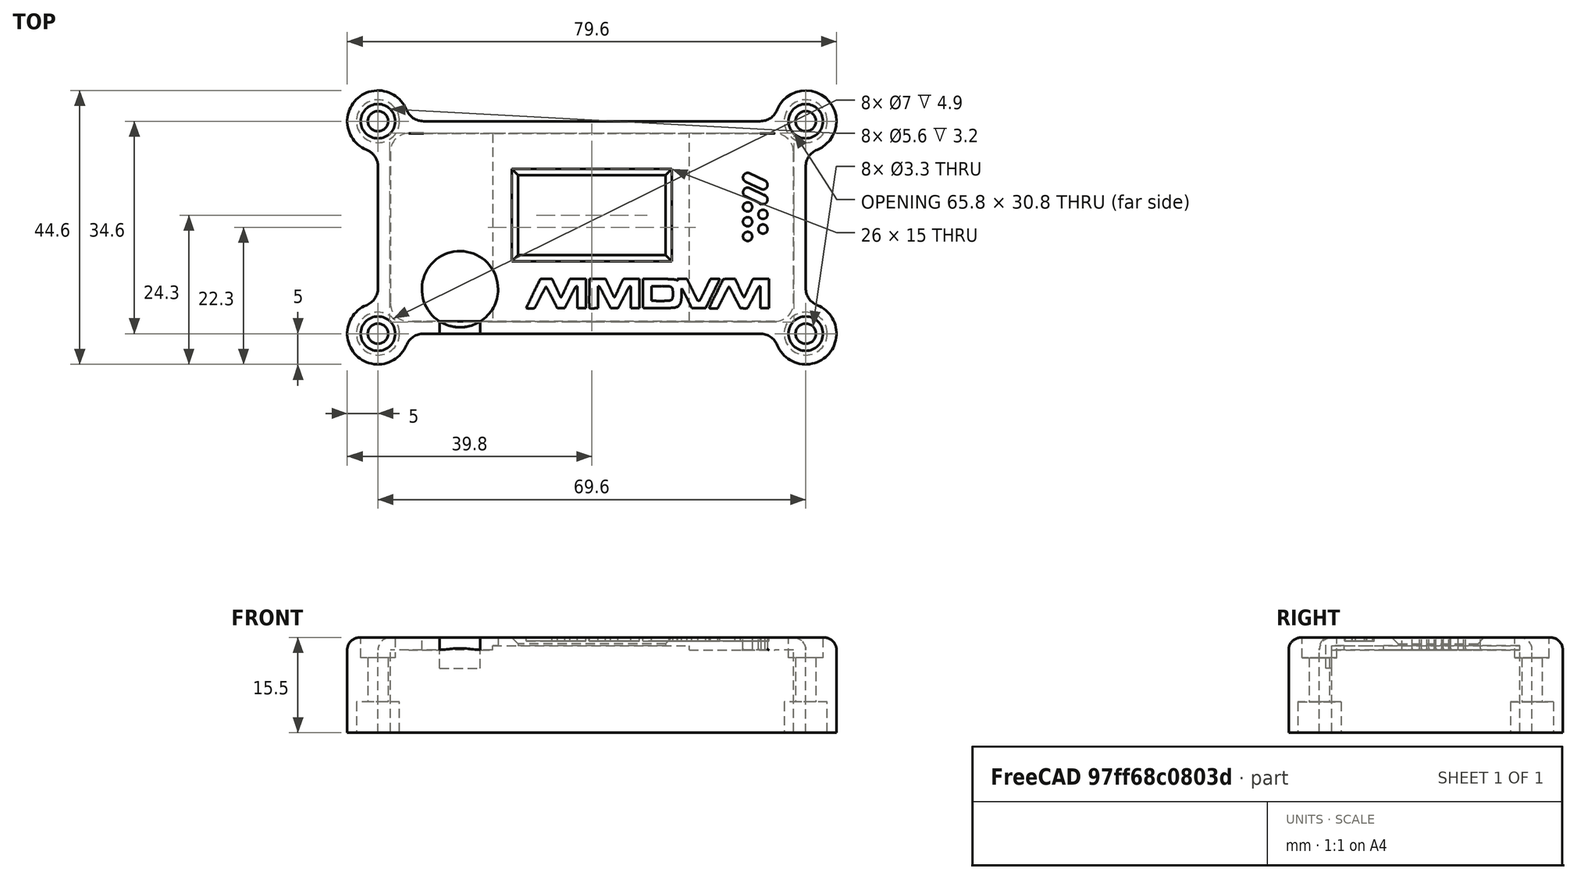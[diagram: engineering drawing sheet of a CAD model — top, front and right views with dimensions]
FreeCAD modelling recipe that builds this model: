
FCSTD DOCUMENT  (FreeCAD 0.18R13964 (Git))
Label: MMDVM_HS_Top-PCB-v1.7
License: CreativeCommons Attribution-NonCommercial-ShareAlike
LicenseURL: http://creativecommons.org/licenses/by-nc-sa/4.0/
objects: Sketcher::SketchObject×10, PartDesign::Pocket×6, Part::Feature×5, PartDesign::Fillet×4, Part::Cut×2, Part::FeaturePython×2, PartDesign::Pad×1, PartDesign::Chamfer×1, PartDesign::Hole×1, Part::MultiFuse×1, PartDesign::Body×1, Part::Extrusion×1, Mesh::Feature×1
note: 43 computed .brp shape members not serialized (recipe doc carries the construction recipe); baked Part::Feature solids carry a one-line shape summary decoded from their .brp

FEATURE [Sketcher::SketchObject] Sketch
  MapMode = 5
  Support = -> [XY_Plane]
  sketch-geometry (24):
    g0: LineSegment [constr] StartX=-32.5 StartY=15 StartZ=0 EndX=32.5 EndY=15 EndZ=0
    g1: LineSegment [constr] StartX=32.5 StartY=15 StartZ=0 EndX=32.5 EndY=-15 EndZ=0
    g2: LineSegment [constr] StartX=32.5 StartY=-15 StartZ=0 EndX=-32.5 EndY=-15 EndZ=0
    g3: LineSegment [constr] StartX=-32.5 StartY=-15 StartZ=0 EndX=-32.5 EndY=15 EndZ=0
    g4: LineSegment [constr] StartX=-29 StartY=11.5 StartZ=0 EndX=29 EndY=11.5 EndZ=0
    g5: LineSegment [constr] StartX=29 StartY=11.5 StartZ=0 EndX=29 EndY=-11.5 EndZ=0
    g6: LineSegment [constr] StartX=29 StartY=-11.5 StartZ=0 EndX=-29 EndY=-11.5 EndZ=0
    g7: LineSegment [constr] StartX=-29 StartY=-11.5 StartZ=0 EndX=-29 EndY=11.5 EndZ=0
    g8: Circle CenterX=-29 CenterY=11.5 CenterZ=0 NormalX=0 NormalY=0 NormalZ=1 AngleXU=0 Radius=1.375
    g9: Circle CenterX=29 CenterY=11.5 CenterZ=0 NormalX=0 NormalY=0 NormalZ=1 AngleXU=0 Radius=1.375
    g10: Circle CenterX=29 CenterY=-11.5 CenterZ=0 NormalX=0 NormalY=0 NormalZ=1 AngleXU=0 Radius=1.375
    g11: Circle CenterX=-29 CenterY=-11.5 CenterZ=0 NormalX=0 NormalY=0 NormalZ=1 AngleXU=0 Radius=1.375
    g12: LineSegment [constr] StartX=-29.5 StartY=12 StartZ=0 EndX=29.5 EndY=12 EndZ=0
    g13: LineSegment [constr] StartX=29.5 StartY=12 StartZ=0 EndX=29.5 EndY=-12 EndZ=0
    g14: LineSegment [constr] StartX=29.5 StartY=-12 StartZ=0 EndX=-29.5 EndY=-12 EndZ=0
    g15: LineSegment [constr] StartX=-29.5 StartY=-12 StartZ=0 EndX=-29.5 EndY=12 EndZ=0
    g16: ArcOfCircle CenterX=-29.5 CenterY=12 CenterZ=0 NormalX=0 NormalY=0 NormalZ=1 AngleXU=0 Radius=3 StartAngle=1.5708 EndAngle=3.1416
    g17: ArcOfCircle CenterX=29.5 CenterY=12 CenterZ=0 NormalX=0 NormalY=0 NormalZ=1 AngleXU=0 Radius=3 StartAngle=1.42077e-07 EndAngle=1.5708
    g18: ArcOfCircle CenterX=29.5 CenterY=-12 CenterZ=0 NormalX=0 NormalY=0 NormalZ=1 AngleXU=0 Radius=3 StartAngle=4.71239 EndAngle=6.28319
    g19: ArcOfCircle CenterX=-29.5 CenterY=-12 CenterZ=0 NormalX=0 NormalY=0 NormalZ=1 AngleXU=0 Radius=3 StartAngle=3.14159 EndAngle=4.71239
    g20: LineSegment StartX=-29.5 StartY=15 StartZ=0 EndX=29.5 EndY=15 EndZ=0
    g21: LineSegment StartX=32.5 StartY=12 StartZ=0 EndX=32.5 EndY=-12 EndZ=0
    g22: LineSegment StartX=29.5 StartY=-15 StartZ=0 EndX=-29.5 EndY=-15 EndZ=0
    g23: LineSegment StartX=-32.5 StartY=-12 StartZ=0 EndX=-32.5 EndY=12 EndZ=0
  constraints (68):
    c: Coincident(g0,g1)
    c: Coincident(g1,g2)
    c: Coincident(g2,g3)
    c: Coincident(g3,g0)
    c: Horizontal(g0)
    c: Horizontal(g2)
    c: Vertical(g1)
    c: Vertical(g3)
    c: DistanceX(g0,g0) = 65
    c: DistanceY(g1,g1) = 30
    c: Symmetric(g0,g0,g-2)
    c: Symmetric(g0,g1,g-1)
    c: Coincident(g4,g5)
    c: Coincident(g5,g6)
    c: Coincident(g6,g7)
    c: Coincident(g7,g4)
    c: Horizontal(g4)
    c: Horizontal(g6)
    c: Vertical(g5)
    c: Vertical(g7)
    c: DistanceX(g4,g4) = 58
    c: DistanceY(g5,g5) = 23
    c: Symmetric(g4,g5,g-1)
    c: Symmetric(g4,g4,g-2)
    c: Coincident(g8,g4)
    c: Coincident(g9,g4)
    c: Coincident(g10,g5)
    c: Coincident(g11,g6)
    c: Radius(g11) = 1.375
    c: Radius(g8) = 1.375
    c: Radius(g9) = 1.375
    c: Radius(g10) = 1.375
    c: Coincident(g12,g13)
    c: Coincident(g13,g14)
    c: Coincident(g14,g15)
    c: Coincident(g15,g12)
    c: Horizontal(g12)
    c: Horizontal(g14)
    c: Vertical(g13)
    c: Vertical(g15)
    c: DistanceX(g4,g12) = 0.5
    c: DistanceY(g4,g12) = 0.5
    c: DistanceY(g13,g5) = 0.5
    c: DistanceX(g14,g6) = 0.5
    c: Coincident(g16,g12)
    c: Radius(g16) = 3
    c: Coincident(g17,g12)
    c: Radius(g17) = 3
    c: Coincident(g18,g13)
    c: Radius(g18) = 3
    c: Coincident(g19,g14)
    c: Radius(g19) = 3
    c: PointOnObject(g16,g0)
    c: PointOnObject(g17,g1)
    c: PointOnObject(g18,g2)
    c: PointOnObject(g19,g3)
    c: Coincident(g20,g16)
    c: Horizontal(g20)
    c: Coincident(g20,g17)
    c: Coincident(g21,g17)
    c: Vertical(g21)
    c: Coincident(g18,g21)
    c: Coincident(g22,g18)
    c: Horizontal(g22)
    c: Coincident(g19,g22)
    c: Coincident(g23,g19)
    c: Vertical(g23)
    c: Coincident(g23,g16)
FEATURE [Sketcher::SketchObject] Sketch001
  MapMode = 5
  Support = -> [XY_Plane]
  expr: Constraints[8] = Sketch.Constraints[8]
  expr: Constraints[41] = Sketch.Constraints[41]
  expr: Constraints[9] = Sketch.Constraints[9]
  expr: Constraints[45] = Sketch.Constraints[45]
  expr: Constraints[43] = Sketch.Constraints[43]
  expr: Constraints[42] = Sketch.Constraints[42]
  expr: Constraints[20] = Sketch.Constraints[20]
  expr: Constraints[21] = Sketch.Constraints[21]
  expr: Constraints[28] = Sketch.Constraints[28]
  expr: Constraints[29] = Sketch.Constraints[29]
  expr: Constraints[30] = Sketch.Constraints[30]
  expr: Constraints[40] = Sketch.Constraints[40]
  expr: Constraints[31] = Sketch.Constraints[31]
  expr: Constraints[47] = Sketch.Constraints[47]
  expr: Constraints[49] = Sketch.Constraints[49]
  expr: Constraints[51] = Sketch.Constraints[51]
  sketch-geometry (64):
    g0: LineSegment [constr] StartX=-32.5 StartY=15 StartZ=0 EndX=32.5 EndY=15 EndZ=0
    g1: LineSegment [constr] StartX=32.5 StartY=15 StartZ=0 EndX=32.5 EndY=-15 EndZ=0
    g2: LineSegment [constr] StartX=32.5 StartY=-15 StartZ=0 EndX=-32.5 EndY=-15 EndZ=0
    g3: LineSegment [constr] StartX=-32.5 StartY=-15 StartZ=0 EndX=-32.5 EndY=15 EndZ=0
    g4: LineSegment [constr] StartX=-29 StartY=11.5 StartZ=0 EndX=29 EndY=11.5 EndZ=0
    g5: LineSegment [constr] StartX=29 StartY=11.5 StartZ=0 EndX=29 EndY=-11.5 EndZ=0
    g6: LineSegment [constr] StartX=29 StartY=-11.5 StartZ=0 EndX=-29 EndY=-11.5 EndZ=0
    g7: LineSegment [constr] StartX=-29 StartY=-11.5 StartZ=0 EndX=-29 EndY=11.5 EndZ=0
    g8: Circle [constr] CenterX=-29 CenterY=11.5 CenterZ=0 NormalX=0 NormalY=0 NormalZ=1 AngleXU=0 Radius=1.375
    g9: Circle [constr] CenterX=29 CenterY=11.5 CenterZ=0 NormalX=0 NormalY=0 NormalZ=1 AngleXU=0 Radius=1.375
    g10: Circle [constr] CenterX=29 CenterY=-11.5 CenterZ=0 NormalX=0 NormalY=0 NormalZ=1 AngleXU=0 Radius=1.375
    g11: Circle [constr] CenterX=-29 CenterY=-11.5 CenterZ=0 NormalX=0 NormalY=0 NormalZ=1 AngleXU=0 Radius=1.375
    g12: LineSegment [constr] StartX=-29.5 StartY=12 StartZ=0 EndX=29.5 EndY=12 EndZ=0
    g13: LineSegment [constr] StartX=29.5 StartY=12 StartZ=0 EndX=29.5 EndY=-12 EndZ=0
    g14: LineSegment [constr] StartX=29.5 StartY=-12 StartZ=0 EndX=-29.5 EndY=-12 EndZ=0
    g15: LineSegment [constr] StartX=-29.5 StartY=-12 StartZ=0 EndX=-29.5 EndY=12 EndZ=0
    g16: ArcOfCircle [constr] CenterX=-29.5 CenterY=12 CenterZ=0 NormalX=0 NormalY=0 NormalZ=1 AngleXU=0 Radius=3 StartAngle=1.5708 EndAngle=3.14159
    g17: ArcOfCircle [constr] CenterX=29.5 CenterY=12 CenterZ=0 NormalX=0 NormalY=0 NormalZ=1 AngleXU=0 Radius=3 StartAngle=2.8425e-08 EndAngle=1.5708
    g18: ArcOfCircle [constr] CenterX=29.5 CenterY=-12 CenterZ=0 NormalX=0 NormalY=0 NormalZ=1 AngleXU=0 Radius=3 StartAngle=4.71239 EndAngle=6.28319
    g19: ArcOfCircle [constr] CenterX=-29.5 CenterY=-12 CenterZ=0 NormalX=0 NormalY=0 NormalZ=1 AngleXU=0 Radius=3 StartAngle=3.14159 EndAngle=4.71239
    g20: LineSegment [constr] StartX=-29.5 StartY=15 StartZ=0 EndX=29.5 EndY=15 EndZ=0
    g21: LineSegment [constr] StartX=32.5 StartY=12 StartZ=0 EndX=32.5 EndY=-12 EndZ=0
    g22: LineSegment [constr] StartX=29.5 StartY=-15 StartZ=0 EndX=-29.5 EndY=-15 EndZ=0
    g23: LineSegment [constr] StartX=-32.5 StartY=-12 StartZ=0 EndX=-32.5 EndY=12 EndZ=0
    g24: ArcOfCircle [constr] CenterX=-29.5 CenterY=12 CenterZ=0 NormalX=0 NormalY=0 NormalZ=1 AngleXU=0 Radius=3.3 StartAngle=1.5708 EndAngle=3.14159
    g25: ArcOfCircle [constr] CenterX=29.5 CenterY=12 CenterZ=0 NormalX=0 NormalY=0 NormalZ=1 AngleXU=0 Radius=3.3 StartAngle=-2.2e-10 EndAngle=1.5708
    g26: ArcOfCircle [constr] CenterX=29.5 CenterY=-12 CenterZ=0 NormalX=0 NormalY=0 NormalZ=1 AngleXU=0 Radius=3.3 StartAngle=4.71239 EndAngle=6.28319
    g27: ArcOfCircle [constr] CenterX=-29.5 CenterY=-12 CenterZ=0 NormalX=0 NormalY=0 NormalZ=1 AngleXU=0 Radius=3.3 StartAngle=3.14159 EndAngle=4.71239
    g28: LineSegment [constr] StartX=-32.8 StartY=12 StartZ=0 EndX=-32.8 EndY=-12 EndZ=0
    g29: LineSegment [constr] StartX=-29.5 StartY=15.3 StartZ=0 EndX=29.5 EndY=15.3 EndZ=0
    g30: LineSegment [constr] StartX=32.8 StartY=12 StartZ=0 EndX=32.8 EndY=-12 EndZ=0
    g31: LineSegment [constr] StartX=29.5 StartY=-15.3 StartZ=0 EndX=-29.5 EndY=-15.3 EndZ=0
    g32: LineSegment [constr] StartX=-34.8 StartY=17.3 StartZ=0 EndX=34.8 EndY=17.3 EndZ=0
    g33: LineSegment [constr] StartX=34.8 StartY=17.3 StartZ=0 EndX=34.8 EndY=-17.3 EndZ=0
    g34: LineSegment [constr] StartX=34.8 StartY=-17.3 StartZ=0 EndX=-34.8 EndY=-17.3 EndZ=0
    g35: LineSegment [constr] StartX=-34.8 StartY=-17.3 StartZ=0 EndX=-34.8 EndY=17.3 EndZ=0
    g36: Circle [constr] CenterX=34.8 CenterY=17.3 CenterZ=0 NormalX=0 NormalY=0 NormalZ=1 AngleXU=0 Radius=5
    g37: Circle [constr] CenterX=34.8 CenterY=-17.3 CenterZ=0 NormalX=0 NormalY=0 NormalZ=1 AngleXU=0 Radius=5
    g38: Circle [constr] CenterX=-34.8 CenterY=-17.3 CenterZ=0 NormalX=0 NormalY=0 NormalZ=1 AngleXU=0 Radius=5
    g39: Circle [constr] CenterX=-34.8 CenterY=17.3 CenterZ=0 NormalX=0 NormalY=0 NormalZ=1 AngleXU=0 Radius=5
    g40: Circle [constr] CenterX=27.3838 CenterY=20.3 CenterZ=0 NormalX=0 NormalY=0 NormalZ=1 AngleXU=0 Radius=3
    g41: Circle [constr] CenterX=-27.3838 CenterY=20.3 CenterZ=0 NormalX=0 NormalY=0 NormalZ=1 AngleXU=0 Radius=3
    g42: Circle [constr] CenterX=-37.8 CenterY=9.8838 CenterZ=0 NormalX=0 NormalY=0 NormalZ=1 AngleXU=0 Radius=3
    g43: Circle [constr] CenterX=-37.8 CenterY=-9.8838 CenterZ=0 NormalX=0 NormalY=0 NormalZ=1 AngleXU=0 Radius=3
    g44: Circle [constr] CenterX=-27.3838 CenterY=-20.3 CenterZ=0 NormalX=0 NormalY=0 NormalZ=1 AngleXU=0 Radius=3
    g45: Circle [constr] CenterX=27.3838 CenterY=-20.3 CenterZ=0 NormalX=0 NormalY=0 NormalZ=1 AngleXU=0 Radius=3
    g46: Circle [constr] CenterX=37.8 CenterY=-9.8838 CenterZ=0 NormalX=0 NormalY=0 NormalZ=1 AngleXU=0 Radius=3
    g47: Circle [constr] CenterX=37.8 CenterY=9.8838 CenterZ=0 NormalX=0 NormalY=0 NormalZ=1 AngleXU=0 Radius=3
    g48: ArcOfCircle CenterX=34.8 CenterY=17.3 CenterZ=0 NormalX=0 NormalY=0 NormalZ=1 AngleXU=0 Radius=5 StartAngle=5.09679 EndAngle=9.04038
    g49: ArcOfCircle CenterX=27.3838 CenterY=20.3 CenterZ=0 NormalX=0 NormalY=0 NormalZ=1 AngleXU=0 Radius=3 StartAngle=4.71239 EndAngle=5.89879
    g50: ArcOfCircle CenterX=37.8 CenterY=9.8838 CenterZ=0 NormalX=0 NormalY=0 NormalZ=1 AngleXU=0 Radius=3 StartAngle=1.95519 EndAngle=3.14159
    g51: ArcOfCircle CenterX=37.8 CenterY=-9.8838 CenterZ=0 NormalX=0 NormalY=0 NormalZ=1 AngleXU=0 Radius=3 StartAngle=3.14159 EndAngle=4.32799
    g52: ArcOfCircle CenterX=34.8 CenterY=-17.3 CenterZ=0 NormalX=0 NormalY=0 NormalZ=1 AngleXU=0 Radius=5 StartAngle=3.52599 EndAngle=7.46958
    g53: ArcOfCircle CenterX=27.3838 CenterY=-20.3 CenterZ=0 NormalX=0 NormalY=0 NormalZ=1 AngleXU=0 Radius=3 StartAngle=0.384397 EndAngle=1.5708
    g54: ArcOfCircle CenterX=-27.3838 CenterY=-20.3 CenterZ=0 NormalX=0 NormalY=0 NormalZ=1 AngleXU=0 Radius=3 StartAngle=1.5708 EndAngle=2.7572
    g55: ArcOfCircle CenterX=-34.8 CenterY=-17.3 CenterZ=0 NormalX=0 NormalY=0 NormalZ=1 AngleXU=0 Radius=5 StartAngle=1.95519 EndAngle=5.89879
    g56: ArcOfCircle CenterX=-37.8 CenterY=-9.8838 CenterZ=0 NormalX=0 NormalY=0 NormalZ=1 AngleXU=0 Radius=3 StartAngle=5.09679 EndAngle=6.28319
    g57: ArcOfCircle CenterX=-37.8 CenterY=9.8838 CenterZ=0 NormalX=0 NormalY=0 NormalZ=1 AngleXU=0 Radius=3 StartAngle=6.28319 EndAngle=7.46958
    g58: ArcOfCircle CenterX=-34.8 CenterY=17.3 CenterZ=0 NormalX=0 NormalY=0 NormalZ=1 AngleXU=0 Radius=5 StartAngle=0.384397 EndAngle=4.32799
    g59: ArcOfCircle CenterX=-27.3838 CenterY=20.3 CenterZ=0 NormalX=0 NormalY=0 NormalZ=1 AngleXU=0 Radius=3 StartAngle=3.52599 EndAngle=4.71239
    g60: LineSegment StartX=-27.3838 StartY=17.3 StartZ=0 EndX=27.3838 EndY=17.3 EndZ=0
    g61: LineSegment StartX=34.8 StartY=9.8838 StartZ=0 EndX=34.8 EndY=-9.8838 EndZ=0
    g62: LineSegment StartX=27.3838 StartY=-17.3 StartZ=0 EndX=-27.3838 EndY=-17.3 EndZ=0
    g63: LineSegment StartX=-34.8 StartY=-9.8838 StartZ=0 EndX=-34.8 EndY=9.8838 EndZ=0
  constraints (184):
    c: Coincident(g0,g1)
    c: Coincident(g1,g2)
    c: Coincident(g2,g3)
    c: Coincident(g3,g0)
    c: Horizontal(g0)
    c: Horizontal(g2)
    c: Vertical(g1)
    c: Vertical(g3)
    c: DistanceX(g0,g0) = 65
    c: DistanceY(g1,g1) = 30
    c: Symmetric(g0,g0,g-2)
    c: Symmetric(g0,g1,g-1)
    c: Coincident(g4,g5)
    c: Coincident(g5,g6)
    c: Coincident(g6,g7)
    c: Coincident(g7,g4)
    c: Horizontal(g4)
    c: Horizontal(g6)
    c: Vertical(g5)
    c: Vertical(g7)
    c: DistanceX(g4,g4) = 58
    c: DistanceY(g5,g5) = 23
    c: Symmetric(g4,g5,g-1)
    c: Symmetric(g4,g4,g-2)
    c: Coincident(g8,g4)
    c: Coincident(g9,g4)
    c: Coincident(g10,g5)
    c: Coincident(g11,g6)
    c: Radius(g11) = 1.375
    c: Radius(g8) = 1.375
    c: Radius(g9) = 1.375
    c: Radius(g10) = 1.375
    c: Coincident(g12,g13)
    c: Coincident(g13,g14)
    c: Coincident(g14,g15)
    c: Coincident(g15,g12)
    c: Horizontal(g12)
    c: Horizontal(g14)
    c: Vertical(g13)
    c: Vertical(g15)
    c: DistanceX(g4,g12) = 0.5
    c: DistanceY(g4,g12) = 0.5
    c: DistanceY(g13,g5) = 0.5
    c: DistanceX(g14,g6) = 0.5
    c: Coincident(g16,g12)
    c: Radius(g16) = 3
    c: Coincident(g17,g12)
    c: Radius(g17) = 3
    c: Coincident(g18,g13)
    c: Radius(g18) = 3
    c: Coincident(g19,g14)
    c: Radius(g19) = 3
    c: PointOnObject(g16,g0)
    c: PointOnObject(g17,g1)
    c: PointOnObject(g18,g2)
    c: PointOnObject(g19,g3)
    c: Coincident(g20,g16)
    c: Horizontal(g20)
    c: Coincident(g20,g17)
    c: Coincident(g21,g17)
    c: Vertical(g21)
    c: Coincident(g18,g21)
    c: Coincident(g22,g18)
    c: Horizontal(g22)
    c: Coincident(g19,g22)
    c: Coincident(g23,g19)
    c: Vertical(g23)
    c: Coincident(g23,g16)
    c: Coincident(g24,g12)
    c: Radius(g24) = 3.3
    c: Coincident(g25,g12)
    c: Radius(g25) = 3.3
    c: Coincident(g26,g13)
    c: Radius(g26) = 3.3
    c: Coincident(g27,g14)
    c: Radius(g27) = 3.3
    c: Vertical(g28)
    c: DistanceX(g28,g2) = 0.3
    c: Coincident(g27,g28)
    c: Coincident(g28,g24)
    c: Horizontal(g29)
    c: DistanceY(g0,g29) = 0.3
    c: Coincident(g24,g29)
    c: Coincident(g25,g29)
    c: Vertical(g30)
    c: DistanceX(g0,g30) = 0.3
    c: Coincident(g25,g30)
    c: Coincident(g30,g26)
    c: Horizontal(g31)
    c: DistanceY(g31,g1) = 0.3
    c: Coincident(g31,g26)
    c: Coincident(g31,g27)
    c: Coincident(g32,g33)
    c: Coincident(g33,g34)
    c: Coincident(g34,g35)
    c: Coincident(g35,g32)
    c: Horizontal(g32)
    c: Horizontal(g34)
    c: Vertical(g33)
    c: Vertical(g35)
    c: DistanceY(g25,g32) = 2
    c: DistanceX(g25,g32) = 2
    c: DistanceY(g33,g26) = 2
    c: DistanceX(g34,g27) = 2
    c: Coincident(g36,g32)
    c: Coincident(g37,g33)
    c: Coincident(g38,g34)
    c: Coincident(g39,g32)
    c: Radius(g39) = 5
    c: Radius(g38) = 5
    c: Radius(g37) = 5
    c: Radius(g36) = 5
    c: Radius(g40) = 3
    c: Tangent(g40,g36)
    c: Tangent(g40,g32)
    c: Tangent(g47,g36)
    c: Radius(g47) = 3
    c: Tangent(g47,g33)
    c: Radius(g46) = 3
    c: Tangent(g46,g37)
    c: Tangent(g46,g33)
    c: Radius(g45) = 3
    c: Tangent(g45,g37)
    c: Tangent(g45,g34)
    c: Radius(g44) = 3
    c: Tangent(g44,g34)
    c: Tangent(g44,g38)
    c: Radius(g43) = 3
    c: Tangent(g43,g38)
    c: Tangent(g43,g35)
    c: Radius(g42) = 3
    c: Tangent(g42,g35)
    c: Tangent(g42,g39)
    c: Radius(g41) = 3
    c: Tangent(g41,g32)
    c: Tangent(g41,g39)
    c: Coincident(g48,g32)
    c: PointOnObject(g48,g36)
    c: Coincident(g49,g40)
    c: PointOnObject(g49,g40)
    c: Coincident(g50,g47)
    c: PointOnObject(g50,g47)
    c: Coincident(g51,g46)
    c: PointOnObject(g51,g46)
    c: Coincident(g52,g33)
    c: PointOnObject(g52,g37)
    c: Coincident(g53,g45)
    c: PointOnObject(g53,g45)
    c: Coincident(g54,g44)
    c: PointOnObject(g54,g44)
    c: Coincident(g55,g34)
    c: PointOnObject(g55,g38)
    c: Coincident(g56,g43)
    c: PointOnObject(g56,g43)
    c: Coincident(g57,g42)
    c: PointOnObject(g57,g42)
    c: Coincident(g58,g32)
    c: PointOnObject(g58,g39)
    c: Coincident(g59,g41)
    c: PointOnObject(g59,g41)
    c: Coincident(g49,g48)
    c: Coincident(g48,g50)
    c: Coincident(g51,g52)
    c: Coincident(g52,g53)
    c: Coincident(g54,g55)
    c: Coincident(g55,g56)
    c: Coincident(g57,g58)
    c: Coincident(g58,g59)
    c: PointOnObject(g60,g32)
    c: Horizontal(g60)
    c: PointOnObject(g61,g33)
    c: Vertical(g61)
    c: PointOnObject(g62,g34)
    c: Horizontal(g62)
    c: PointOnObject(g63,g35)
    c: Vertical(g63)
    c: Coincident(g59,g60)
    c: Coincident(g60,g49)
    c: Coincident(g50,g61)
    c: Coincident(g61,g51)
    c: Coincident(g53,g62)
    c: Coincident(g54,g62)
    c: Coincident(g56,g63)
    c: Coincident(g57,g63)
FEATURE [PartDesign::Pad] Pad
  Length = 15.5
  Length2 = 100
  Profile = -> Sketch001
  Type = 0
FEATURE [Sketcher::SketchObject] Sketch002
  ExternalGeometry = -> [Pad]
  MapMode = 5
  Placement = pos=(0,0,0) rot=(1,0,0;3.14159rad)
  Support = -> [Pad]
  sketch-geometry (4):
    g0: Circle CenterX=34.8 CenterY=17.3 CenterZ=0 NormalX=0 NormalY=0 NormalZ=1 AngleXU=0 Radius=3.5
    g1: Circle CenterX=34.8 CenterY=-17.3 CenterZ=0 NormalX=0 NormalY=0 NormalZ=1 AngleXU=0 Radius=3.5
    g2: Circle CenterX=-34.8 CenterY=-17.3 CenterZ=0 NormalX=0 NormalY=0 NormalZ=1 AngleXU=0 Radius=3.5
    g3: Circle CenterX=-34.8 CenterY=17.3 CenterZ=0 NormalX=0 NormalY=0 NormalZ=1 AngleXU=0 Radius=3.5
  constraints (8):
    c: Coincident(g0,g-3)
    c: Radius(g0) = 3.5
    c: Coincident(g1,g-6)
    c: Radius(g1) = 3.5
    c: Coincident(g2,g-5)
    c: Radius(g2) = 3.5
    c: Coincident(g3,g-4)
    c: Radius(g3) = 3.5
FEATURE [PartDesign::Pocket] Pocket
  BaseFeature = -> Pad
  Length = 5
  Length2 = 100
  Profile = -> Sketch002
  Type = 0
FEATURE [Sketcher::SketchObject] Sketch003
  MapMode = 5
  Placement = pos=(0,0,0) rot=(1,0,0;3.14159rad)
  Support = -> [Pocket]
  expr: Constraints[8] = Sketch.Constraints[8]
  expr: Constraints[39] = Sketch.Constraints[40]
  expr: Constraints[30] = Sketch.Constraints[31]
  expr: Constraints[27] = Sketch.Constraints[28]
  expr: Constraints[29] = Sketch.Constraints[30]
  expr: Constraints[28] = Sketch.Constraints[29]
  expr: Constraints[20] = -Sketch.Constraints[21]
  expr: Constraints[19] = Sketch.Constraints[20]
  expr: Constraints[42] = Sketch.Constraints[43]
  expr: Constraints[41] = -Sketch.Constraints[42]
  expr: Constraints[9] = -Sketch.Constraints[9]
  expr: Constraints[40] = -Sketch.Constraints[41]
  sketch-geometry (32):
    g0: LineSegment [constr] StartX=-32.5 StartY=-15 StartZ=0 EndX=32.5 EndY=-15 EndZ=0
    g1: LineSegment [constr] StartX=32.5 StartY=-15 StartZ=0 EndX=32.5 EndY=15 EndZ=0
    g2: LineSegment [constr] StartX=32.5 StartY=15 StartZ=0 EndX=-32.5 EndY=15 EndZ=0
    g3: LineSegment [constr] StartX=-32.5 StartY=15 StartZ=0 EndX=-32.5 EndY=-15 EndZ=0
    g4: LineSegment [constr] StartX=-29 StartY=-11.5 StartZ=0 EndX=29 EndY=-11.5 EndZ=0
    g5: LineSegment [constr] StartX=29 StartY=-11.5 StartZ=0 EndX=29 EndY=11.5 EndZ=0
    g6: LineSegment [constr] StartX=29 StartY=11.5 StartZ=0 EndX=-29 EndY=11.5 EndZ=0
    g7: LineSegment [constr] StartX=-29 StartY=11.5 StartZ=0 EndX=-29 EndY=-11.5 EndZ=0
    g8: Circle [constr] CenterX=-29 CenterY=-11.5 CenterZ=0 NormalX=0 NormalY=0 NormalZ=1 AngleXU=0 Radius=1.375
    g9: Circle [constr] CenterX=29 CenterY=-11.5 CenterZ=0 NormalX=0 NormalY=0 NormalZ=1 AngleXU=0 Radius=1.375
    g10: Circle [constr] CenterX=29 CenterY=11.5 CenterZ=0 NormalX=0 NormalY=0 NormalZ=1 AngleXU=0 Radius=1.375
    g11: Circle [constr] CenterX=-29 CenterY=11.5 CenterZ=0 NormalX=0 NormalY=0 NormalZ=1 AngleXU=0 Radius=1.375
    g12: LineSegment [constr] StartX=-29.5 StartY=-12 StartZ=0 EndX=29.5 EndY=-12 EndZ=0
    g13: LineSegment [constr] StartX=29.5 StartY=-12 StartZ=0 EndX=29.5 EndY=12 EndZ=0
    g14: LineSegment [constr] StartX=29.5 StartY=12 StartZ=0 EndX=-29.5 EndY=12 EndZ=0
    g15: LineSegment [constr] StartX=-29.5 StartY=12 StartZ=0 EndX=-29.5 EndY=-12 EndZ=0
    g16: LineSegment [constr] StartX=-29.5121 StartY=-15 StartZ=0 EndX=29.5 EndY=-15 EndZ=0
    g17: LineSegment [constr] StartX=32.5 StartY=-12 StartZ=0 EndX=32.5 EndY=12 EndZ=0
    g18: LineSegment [constr] StartX=29.5 StartY=15 StartZ=0 EndX=-29.5121 EndY=15 EndZ=0
    g19: LineSegment [constr] StartX=-32.5 StartY=12 StartZ=0 EndX=-32.5 EndY=-12 EndZ=0
    g20: ArcOfCircle [constr] CenterX=-29.5 CenterY=12 CenterZ=0 NormalX=0 NormalY=0 NormalZ=1 AngleXU=0 Radius=3.00002 StartAngle=1.57483 EndAngle=3.1416
    g21: ArcOfCircle [constr] CenterX=29.5 CenterY=12 CenterZ=0 NormalX=0 NormalY=0 NormalZ=1 AngleXU=0 Radius=3 StartAngle=6.28318 EndAngle=7.85399
    g22: ArcOfCircle [constr] CenterX=29.5 CenterY=-12 CenterZ=0 NormalX=0 NormalY=0 NormalZ=1 AngleXU=0 Radius=3 StartAngle=4.71238 EndAngle=6.28319
    g23: ArcOfCircle [constr] CenterX=-29.5 CenterY=-12 CenterZ=0 NormalX=0 NormalY=0 NormalZ=1 AngleXU=0 Radius=3.00002 StartAngle=3.14159 EndAngle=4.70836
    g24: LineSegment StartX=-29.8 StartY=15.3 StartZ=0 EndX=29.8 EndY=15.3 EndZ=0
    g25: LineSegment StartX=32.8 StartY=12.3 StartZ=0 EndX=32.8 EndY=-12.3 EndZ=0
    g26: LineSegment StartX=29.8 StartY=-15.3 StartZ=0 EndX=-29.8 EndY=-15.3 EndZ=0
    g27: LineSegment StartX=-32.8 StartY=-12.3 StartZ=0 EndX=-32.8 EndY=12.3 EndZ=0
    g28: ArcOfCircle CenterX=29.8 CenterY=12.3 CenterZ=0 NormalX=0 NormalY=0 NormalZ=1 AngleXU=0 Radius=3 StartAngle=0 EndAngle=1.5708
    g29: ArcOfCircle CenterX=29.8 CenterY=-12.3 CenterZ=0 NormalX=0 NormalY=0 NormalZ=1 AngleXU=0 Radius=3 StartAngle=4.71239 EndAngle=6.28319
    g30: ArcOfCircle CenterX=-29.8 CenterY=-12.3 CenterZ=0 NormalX=0 NormalY=0 NormalZ=1 AngleXU=0 Radius=3 StartAngle=3.14159 EndAngle=4.71239
    g31: ArcOfCircle CenterX=-29.8 CenterY=12.3 CenterZ=0 NormalX=0 NormalY=0 NormalZ=1 AngleXU=0 Radius=3 StartAngle=1.5708 EndAngle=3.14159
  constraints (83):
    c: Coincident(g0,g1)
    c: Coincident(g1,g2)
    c: Coincident(g2,g3)
    c: Coincident(g3,g0)
    c: Horizontal(g0)
    c: Horizontal(g2)
    c: Vertical(g1)
    c: Vertical(g3)
    c: DistanceX(g0,g0) = 65
    c: DistanceY(g1,g1) = -30
    c: Symmetric(g0,g0,g-2)
    c: Symmetric(g0,g1,g-1)
    c: Coincident(g4,g5)
    c: Coincident(g5,g6)
    c: Coincident(g6,g7)
    c: Horizontal(g4)
    c: Horizontal(g6)
    c: Vertical(g5)
    c: Vertical(g7)
    c: DistanceX(g4,g4) = 58
    c: DistanceY(g5,g5) = -23
    c: Symmetric(g4,g5,g-1)
    c: Symmetric(g4,g4,g-2)
    c: Coincident(g8,g4)
    c: Coincident(g9,g4)
    c: Coincident(g10,g5)
    c: Coincident(g11,g6)
    c: Radius(g11) = 1.375
    c: Radius(g8) = 1.375
    c: Radius(g9) = 1.375
    c: Radius(g10) = 1.375
    c: Coincident(g12,g13)
    c: Coincident(g13,g14)
    c: Coincident(g14,g15)
    c: Coincident(g15,g12)
    c: Horizontal(g12)
    c: Horizontal(g14)
    c: Vertical(g13)
    c: Vertical(g15)
    c: DistanceX(g4,g12) = 0.5
    c: DistanceY(g4,g12) = -0.5
    c: DistanceY(g13,g5) = -0.5
    c: DistanceX(g14,g6) = 0.5
    c: PointOnObject(g16,g0)
    c: PointOnObject(g17,g1)
    c: PointOnObject(g18,g2)
    c: PointOnObject(g19,g3)
    c: Horizontal(g16)
    c: Vertical(g17)
    c: Horizontal(g18)
    c: Vertical(g19)
    c: Coincident(g20,g14)
    c: Coincident(g20,g18)
    c: Coincident(g20,g19)
    c: Coincident(g21,g13)
    c: Coincident(g21,g17)
    c: Coincident(g21,g18)
    c: Coincident(g22,g12)
    c: Coincident(g22,g16)
    c: Coincident(g22,g17)
    c: Coincident(g23,g12)
    c: Coincident(g23,g19)
    c: Coincident(g23,g16)
    c: Horizontal(g24)
    c: Horizontal(g26)
    c: Vertical(g25)
    c: Vertical(g27)
    c: Tangent(g24,g28) = 1.5708
    c: Tangent(g25,g28) = 1.5708
    c: Tangent(g25,g29) = 1.5708
    c: Tangent(g26,g29) = 1.5708
    c: Tangent(g26,g30) = 1.5708
    c: Tangent(g27,g30) = 1.5708
    c: Tangent(g27,g31) = 1.5708
    c: Tangent(g24,g31) = 1.5708
    c: Radius(g31) = 3
    c: Radius(g28) = 3
    c: Radius(g29) = 3
    c: Radius(g30) = 3
    c: DistanceY(g1,g24) = 0.3
    c: DistanceX(g17,g25) = 0.3
    c: DistanceY(g26,g16) = 0.3
    c: DistanceX(g27,g19) = 0.3
FEATURE [PartDesign::Pocket] Pocket001
  BaseFeature = -> Pocket
  Length = 13.5
  Length2 = 100
  Profile = -> Sketch003
  Type = 0
FEATURE [Sketcher::SketchObject] Sketch004
  ExternalGeometry = -> [Pocket001]
  MapMode = 5
  Placement = pos=(0,0,15.5) rot=(0,0,1;0rad)
  Support = -> [Pocket001]
  sketch-geometry (32):
    g0: LineSegment StartX=-27.3838 StartY=17.3 StartZ=0 EndX=-31.8 EndY=17.3 EndZ=0
    g1: LineSegment StartX=-34.8 StartY=9.8838 StartZ=0 EndX=-34.8 EndY=14.3 EndZ=0
    g2: Circle [constr] CenterX=-31.8 CenterY=14.3 CenterZ=0 NormalX=0 NormalY=0 NormalZ=1 AngleXU=0 Radius=3
    g3: ArcOfCircle CenterX=-31.8 CenterY=14.3 CenterZ=0 NormalX=0 NormalY=0 NormalZ=1 AngleXU=0 Radius=3 StartAngle=1.5708 EndAngle=3.14159
    g4: LineSegment StartX=-41.7809 StartY=24.2149 StartZ=0 EndX=-27.3838 EndY=24.2149 EndZ=0
    g5: LineSegment StartX=-41.7809 StartY=9.8838 StartZ=0 EndX=-41.7809 EndY=24.2149 EndZ=0
    g6: LineSegment StartX=-27.3838 StartY=24.2149 StartZ=0 EndX=-27.3838 EndY=17.3 EndZ=0
    g7: LineSegment StartX=-41.7809 StartY=9.8838 StartZ=0 EndX=-34.8 EndY=9.8838 EndZ=0
    g8: LineSegment StartX=27.3838 StartY=17.3 StartZ=0 EndX=31.8 EndY=17.3 EndZ=0
    g9: LineSegment StartX=34.8 StartY=9.8838 StartZ=0 EndX=34.8 EndY=14.3 EndZ=0
    g10: Circle [constr] CenterX=31.8 CenterY=14.3 CenterZ=0 NormalX=0 NormalY=0 NormalZ=1 AngleXU=0 Radius=3
    g11: ArcOfCircle CenterX=31.8 CenterY=14.3 CenterZ=0 NormalX=0 NormalY=0 NormalZ=1 AngleXU=0 Radius=3 StartAngle=4.4834e-08 EndAngle=1.5708
    g12: LineSegment StartX=41.7622 StartY=24.6512 StartZ=0 EndX=27.3838 EndY=24.6512 EndZ=0
    g13: LineSegment StartX=41.7622 StartY=9.8838 StartZ=0 EndX=41.7622 EndY=24.6512 EndZ=0
    g14: LineSegment StartX=27.3838 StartY=24.6512 StartZ=0 EndX=27.3838 EndY=17.3 EndZ=0
    g15: LineSegment StartX=41.7622 StartY=9.8838 StartZ=0 EndX=34.8 EndY=9.8838 EndZ=0
    g16: LineSegment StartX=-34.8 StartY=-9.8838 StartZ=0 EndX=-34.8 EndY=-14.3 EndZ=0
    g17: LineSegment StartX=-27.3838 StartY=-17.3 StartZ=0 EndX=-31.8 EndY=-17.3 EndZ=0
    g18: Circle [constr] CenterX=-31.8 CenterY=-14.3 CenterZ=0 NormalX=0 NormalY=0 NormalZ=1 AngleXU=0 Radius=3
    g19: ArcOfCircle CenterX=-31.8 CenterY=-14.3 CenterZ=0 NormalX=0 NormalY=0 NormalZ=1 AngleXU=0 Radius=3 StartAngle=3.14159 EndAngle=4.71239
    g20: LineSegment StartX=-27.3838 StartY=-24.2044 StartZ=0 EndX=-41.4724 EndY=-24.2044 EndZ=0
    g21: LineSegment StartX=-41.4724 StartY=-24.2044 StartZ=0 EndX=-41.4724 EndY=-9.8838 EndZ=0
    g22: LineSegment StartX=-41.4724 StartY=-9.8838 StartZ=0 EndX=-34.8 EndY=-9.8838 EndZ=0
    g23: LineSegment StartX=-27.3838 StartY=-24.2044 StartZ=0 EndX=-27.3838 EndY=-17.3 EndZ=0
    g24: LineSegment StartX=34.8 StartY=-9.8838 StartZ=0 EndX=34.8 EndY=-14.3 EndZ=0
    g25: LineSegment StartX=27.3838 StartY=-17.3 StartZ=0 EndX=31.8 EndY=-17.3 EndZ=0
    g26: Circle [constr] CenterX=31.8 CenterY=-14.3 CenterZ=0 NormalX=0 NormalY=0 NormalZ=1 AngleXU=0 Radius=3
    g27: ArcOfCircle CenterX=31.8 CenterY=-14.3 CenterZ=0 NormalX=0 NormalY=0 NormalZ=1 AngleXU=0 Radius=3 StartAngle=4.71239 EndAngle=6.28319
    g28: LineSegment StartX=41.5436 StartY=-23.6904 StartZ=0 EndX=27.3838 EndY=-23.6904 EndZ=0
    g29: LineSegment StartX=41.5436 StartY=-9.8838 StartZ=0 EndX=41.5436 EndY=-23.6904 EndZ=0
    g30: LineSegment StartX=41.5436 StartY=-9.8838 StartZ=0 EndX=34.8 EndY=-9.8838 EndZ=0
    g31: LineSegment StartX=27.3838 StartY=-23.6904 StartZ=0 EndX=27.3838 EndY=-17.3 EndZ=0
  constraints (88):
    c: PointOnObject(g0,g-3)
    c: Horizontal(g0)
    c: PointOnObject(g1,g-6)
    c: Vertical(g1)
    c: Radius(g2) = 3
    c: Tangent(g2,g0)
    c: Tangent(g2,g1)
    c: Coincident(g3,g2)
    c: PointOnObject(g3,g2)
    c: Coincident(g3,g1)
    c: Coincident(g3,g0)
    c: Coincident(g5,g4)
    c: Horizontal(g4)
    c: Vertical(g5)
    c: Coincident(g6,g4)
    c: Vertical(g6)
    c: Coincident(g7,g5)
    c: Horizontal(g7)
    c: Coincident(g7,g1)
    c: Coincident(g6,g0)
    c: PointOnObject(g8,g-3)
    c: Horizontal(g8)
    c: PointOnObject(g9,g-4)
    c: Vertical(g9)
    c: Radius(g10) = 3
    c: Tangent(g10,g8)
    c: Tangent(g10,g9)
    c: Coincident(g11,g10)
    c: PointOnObject(g11,g10)
    c: Coincident(g11,g8)
    c: Coincident(g11,g9)
    c: Coincident(g13,g12)
    c: Horizontal(g12)
    c: Vertical(g13)
    c: Coincident(g14,g12)
    c: Vertical(g14)
    c: Coincident(g15,g13)
    c: Horizontal(g15)
    c: Coincident(g15,g9)
    c: Coincident(g14,g8)
    c: PointOnObject(g16,g-6)
    c: Vertical(g16)
    c: PointOnObject(g17,g-5)
    c: Horizontal(g17)
    c: Radius(g18) = 3
    c: Tangent(g18,g16)
    c: Tangent(g18,g17)
    c: Coincident(g19,g18)
    c: PointOnObject(g19,g18)
    c: Coincident(g19,g17)
    c: Coincident(g19,g16)
    c: Coincident(g20,g21)
    c: Horizontal(g20)
    c: Vertical(g21)
    c: Coincident(g22,g21)
    c: Horizontal(g22)
    c: Coincident(g23,g20)
    c: Vertical(g23)
    c: Coincident(g23,g17)
    c: Coincident(g22,g16)
    c: PointOnObject(g24,g-4)
    c: Vertical(g24)
    c: PointOnObject(g25,g-5)
    c: Horizontal(g25)
    c: Radius(g26) = 3
    c: Tangent(g26,g24)
    c: Tangent(g26,g25)
    c: Coincident(g27,g26)
    c: PointOnObject(g27,g26)
    c: Coincident(g27,g24)
    c: Coincident(g27,g25)
    c: Coincident(g29,g28)
    c: Horizontal(g28)
    c: Vertical(g29)
    c: Coincident(g30,g29)
    c: Horizontal(g30)
    c: Coincident(g31,g28)
    c: Vertical(g31)
    c: Coincident(g31,g25)
    c: Coincident(g30,g24)
    c: Coincident(g0,g-3)
    c: Coincident(g1,g-6)
    c: Coincident(g-6,g16)
    c: Coincident(g17,g-5)
    c: Coincident(g-5,g25)
    c: Coincident(g-4,g24)
    c: Coincident(g9,g-4)
    c: Coincident(g8,g-3)
FEATURE [Sketcher::SketchObject] Sketch005
  ExternalGeometry = -> [Pocket001,Sketch]
  MapMode = 5
  Placement = pos=(0,0,15.5) rot=(0,0,1;0rad)
  Support = -> [Pocket001]
  sketch-geometry (10):
    g0: LineSegment [constr] StartX=-21.4583 StartY=31.2328 StartZ=0 EndX=-21.4583 EndY=-27.0552 EndZ=0
    g1: LineSegment [constr] StartX=-45.4064 StartY=-10.0606 StartZ=0 EndX=40.4454 EndY=-10.0606 EndZ=0
    g2: Circle [constr] CenterX=-21.4583 CenterY=-10.0606 CenterZ=0 NormalX=0 NormalY=0 NormalZ=1 AngleXU=0 Radius=6.2
    g3: LineSegment StartX=-12 StartY=8.5 StartZ=0 EndX=12 EndY=8.5 EndZ=0
    g4: LineSegment StartX=12 StartY=8.5 StartZ=0 EndX=12 EndY=-4.5 EndZ=0
    g5: LineSegment StartX=12 StartY=-4.5 StartZ=0 EndX=-12 EndY=-4.5 EndZ=0
    g6: LineSegment StartX=-12 StartY=-4.5 StartZ=0 EndX=-12 EndY=8.5 EndZ=0
    g7: LineSegment [constr] StartX=-29 StartY=24.9491 StartZ=0 EndX=-29 EndY=-20.674 EndZ=0
    g8: LineSegment [constr] StartX=-44.8443 StartY=11.5 StartZ=0 EndX=14.9752 EndY=11.5 EndZ=0
    g9: Circle CenterX=-21.4583 CenterY=-10.0606 CenterZ=0 NormalX=0 NormalY=0 NormalZ=1 AngleXU=0 Radius=6.2
  constraints (26):
    c: Coincident(g5,g6)
    c: Coincident(g3,g6)
    c: Coincident(g4,g5)
    c: Coincident(g3,g4)
    c: DistanceX(g3,g3) = 24
    c: DistanceY(g4,g4) = 13
    c: Vertical(g7)
    c: Horizontal(g8)
    c: PointOnObject(g-4,g8)
    c: PointOnObject(g-4,g7)
    c: PointOnObject(g2,g0)
    c: PointOnObject(g2,g1)
    c: DistanceX(g7,g0) = 7.54172
    c: DistanceX(g7,g3) = 17
    c: DistanceY(g3,g-4) = 3
    c: DistanceY(g1,g8) = 21.5606
    c: Vertical(g0)
    c: Horizontal(g1)
    c: Radius(g2) = 6.2
    c: Coincident(g9,g2)
    c: Radius(g9) = 6.2
    c: DistanceY(g-5,g-4) = 23
    c: Vertical(g4)
    c: Vertical(g6)
    c: Horizontal(g3)
    c: Horizontal(g5)
FEATURE [PartDesign::Pocket] Pocket002
  BaseFeature = -> Pocket001
  Length = 5
  Length2 = 100
  Profile = -> Sketch005
  Type = 0
FEATURE [Sketcher::SketchObject] Sketch006
  AttachmentOffset = pos=(7.7,0,0) rot=(0,0,1;0rad)
  ExternalGeometry = -> [Pocket002]
  MapMode = 5
  Placement = pos=(7.7,0,13.5) rot=(1,0,0;3.14159rad)
  Support = -> [Pocket002]
  sketch-geometry (4):
    g0: LineSegment StartX=-23.85 StartY=15.3 StartZ=0 EndX=8.15 EndY=15.3 EndZ=0
    g1: LineSegment StartX=8.15 StartY=15.3 StartZ=0 EndX=8.15 EndY=-15.3 EndZ=0
    g2: LineSegment StartX=8.15 StartY=-15.3 StartZ=0 EndX=-23.85 EndY=-15.3 EndZ=0
    g3: LineSegment StartX=-23.85 StartY=-15.3 StartZ=0 EndX=-23.85 EndY=15.3 EndZ=0
FEATURE [PartDesign::Pocket] Pocket003
  BaseFeature = -> Pocket002
  Length = 0.7
  Length2 = 100
  Profile = -> Sketch006
  Type = 0
FEATURE [PartDesign::Fillet] Fillet
  Base = -> Pocket003 [Edge38]
  BaseFeature = -> Pocket003
  Radius = 2
FEATURE [PartDesign::Chamfer] Chamfer
  Base = -> Fillet [Edge60,Edge61,Edge62,Edge63]
  BaseFeature = -> Fillet
  Size = 1
FEATURE [Sketcher::SketchObject] Sketch007
  MapMode = 5
  Placement = pos=(0,0,15.5) rot=(0,0,1;0rad)
  sketch-geometry (4):
    g0: Circle CenterX=34.8 CenterY=17.3 CenterZ=0 NormalX=0 NormalY=0 NormalZ=1 AngleXU=0 Radius=2.63102
    g1: Circle CenterX=-34.8 CenterY=17.3 CenterZ=0 NormalX=0 NormalY=0 NormalZ=1 AngleXU=0 Radius=2.66333
    g2: Circle CenterX=-34.8 CenterY=-17.3 CenterZ=0 NormalX=0 NormalY=0 NormalZ=1 AngleXU=0 Radius=2.82775
    g3: Circle CenterX=34.8 CenterY=-17.3 CenterZ=0 NormalX=0 NormalY=0 NormalZ=1 AngleXU=0 Radius=2.89107
FEATURE [PartDesign::Hole] Hole
  BaseFeature = -> Chamfer
  Depth = 20
  DepthType = 1
  Diameter = 3.3
  DrillPoint = 1
  DrillPointAngle = 118
  HoleCutCountersinkAngle = 90
  HoleCutDepth = 0
  HoleCutDiameter = 3
  HoleCutType = 0
  ModelActualThread = false
  Profile = -> Sketch007
  Tapered = false
  TaperedAngle = 90
  ThreadAngle = 60
  ThreadClass = 0
  ThreadCutOffInner = 0.0433013
  ThreadCutOffOuter = 0.0866025
  ThreadDirection = 0
  ThreadFit = 0
  ThreadPitch = 0.4
  ThreadSize = 3
  ThreadType = 1
  Threaded = false
FEATURE [Sketcher::SketchObject] Sketch008
  ExternalGeometry = -> [Hole]
  MapMode = 5
  Placement = pos=(0,0,15.5) rot=(0,0,1;0rad)
  Support = -> [Hole]
  sketch-geometry (4):
    g0: Circle CenterX=34.8 CenterY=17.3 CenterZ=0 NormalX=0 NormalY=0 NormalZ=1 AngleXU=0 Radius=2.8
    g1: Circle CenterX=34.8 CenterY=-17.3 CenterZ=0 NormalX=0 NormalY=0 NormalZ=1 AngleXU=0 Radius=2.8
    g2: Circle CenterX=-34.8 CenterY=-17.3 CenterZ=0 NormalX=0 NormalY=0 NormalZ=1 AngleXU=0 Radius=2.8
    g3: Circle CenterX=-34.8 CenterY=17.3 CenterZ=0 NormalX=0 NormalY=0 NormalZ=1 AngleXU=0 Radius=2.8
  constraints (7):
    c: Coincident(g0,g-5)
    c: Coincident(g1,g-8)
    c: Coincident(g3,g-6)
    c: Radius(g3) = 2.8
    c: Radius(g0) = 2.8
    c: Radius(g2) = 2.8
    c: Radius(g1) = 2.8
FEATURE [PartDesign::Pocket] Pocket004
  BaseFeature = -> Hole
  Length = 3.3
  Length2 = 100
  Profile = -> Sketch008
  Type = 0
FEATURE [Sketcher::SketchObject] Sketch009
  MapMode = 5
  Placement = pos=(0,0,15.5) rot=(0,0,1;0rad)
  expr: Constraints[7] = Sketch.Constraints[9]
  expr: Constraints[40] = Sketch.Constraints[42]
  expr: Constraints[18] = Sketch.Constraints[20]
  expr: Constraints[19] = Sketch.Constraints[21]
  expr: Constraints[29] = Sketch.Constraints[31]
  expr: Constraints[27] = Sketch.Constraints[29]
  expr: Constraints[28] = Sketch.Constraints[30]
  expr: Constraints[26] = Sketch.Constraints[28]
  expr: Constraints[6] = Sketch.Constraints[8]
  expr: Constraints[38] = Sketch.Constraints[40]
  expr: Constraints[47] = Sketch.Constraints[49]
  expr: Constraints[39] = Sketch.Constraints[41]
  expr: Constraints[49] = Sketch.Constraints[51]
  expr: Constraints[45] = Sketch.Constraints[47]
  expr: Constraints[43] = Sketch.Constraints[45]
  expr: Constraints[41] = Sketch.Constraints[43]
  sketch-geometry (62):
    g0: LineSegment [constr] StartX=-32.5 StartY=15 StartZ=0 EndX=32.5 EndY=15 EndZ=0
    g1: LineSegment [constr] StartX=32.5 StartY=15 StartZ=0 EndX=32.5 EndY=-15 EndZ=0
    g2: LineSegment [constr] StartX=32.5 StartY=-15 StartZ=0 EndX=-32.5 EndY=-15 EndZ=0
    g3: LineSegment [constr] StartX=-32.5 StartY=-15 StartZ=0 EndX=-32.5 EndY=15 EndZ=0
    g4: LineSegment [constr] StartX=-29 StartY=11.5 StartZ=0 EndX=29 EndY=11.5 EndZ=0
    g5: LineSegment [constr] StartX=29 StartY=11.5 StartZ=0 EndX=29 EndY=-11.5 EndZ=0
    g6: LineSegment [constr] StartX=29 StartY=-11.5 StartZ=0 EndX=-29 EndY=-11.5 EndZ=0
    g7: LineSegment [constr] StartX=-29 StartY=-11.5 StartZ=0 EndX=-29 EndY=11.5 EndZ=0
    g8: Circle [constr] CenterX=-29 CenterY=11.5 CenterZ=0 NormalX=0 NormalY=0 NormalZ=1 AngleXU=0 Radius=1.375
    g9: Circle [constr] CenterX=29 CenterY=11.5 CenterZ=0 NormalX=0 NormalY=0 NormalZ=1 AngleXU=0 Radius=1.375
    g10: Circle [constr] CenterX=29 CenterY=-11.5 CenterZ=0 NormalX=0 NormalY=0 NormalZ=1 AngleXU=0 Radius=1.375
    g11: Circle [constr] CenterX=-29 CenterY=-11.5 CenterZ=0 NormalX=0 NormalY=0 NormalZ=1 AngleXU=0 Radius=1.375
    g12: LineSegment [constr] StartX=-29.5 StartY=12 StartZ=0 EndX=29.5 EndY=12 EndZ=0
    g13: LineSegment [constr] StartX=29.5 StartY=12 StartZ=0 EndX=29.5 EndY=-12 EndZ=0
    g14: LineSegment [constr] StartX=29.5 StartY=-12 StartZ=0 EndX=-29.5 EndY=-12 EndZ=0
    g15: LineSegment [constr] StartX=-29.5 StartY=-12 StartZ=0 EndX=-29.5 EndY=12 EndZ=0
    g16: ArcOfCircle [constr] CenterX=-29.5 CenterY=12 CenterZ=0 NormalX=0 NormalY=0 NormalZ=1 AngleXU=0 Radius=3 StartAngle=1.5708 EndAngle=3.14159
    g17: ArcOfCircle [constr] CenterX=29.5 CenterY=12 CenterZ=0 NormalX=0 NormalY=0 NormalZ=1 AngleXU=0 Radius=3 StartAngle=5.0002e-08 EndAngle=1.5708
    g18: ArcOfCircle [constr] CenterX=29.5 CenterY=-12 CenterZ=0 NormalX=0 NormalY=0 NormalZ=1 AngleXU=0 Radius=3 StartAngle=4.71239 EndAngle=6.28319
    g19: ArcOfCircle [constr] CenterX=-29.5 CenterY=-12 CenterZ=0 NormalX=0 NormalY=0 NormalZ=1 AngleXU=0 Radius=3 StartAngle=3.14159 EndAngle=4.71239
    g20: LineSegment [constr] StartX=-29.5 StartY=15 StartZ=0 EndX=29.5 EndY=15 EndZ=0
    g21: LineSegment [constr] StartX=32.5 StartY=12 StartZ=0 EndX=32.5 EndY=-12 EndZ=0
    g22: LineSegment [constr] StartX=29.5 StartY=-15 StartZ=0 EndX=-29.5 EndY=-15 EndZ=0
    g23: LineSegment [constr] StartX=-32.5 StartY=-12 StartZ=0 EndX=-32.5 EndY=12 EndZ=0
    g24: LineSegment [constr] StartX=25.3417 StartY=8.13712 StartZ=0 EndX=27.8417 EndY=8.13712 EndZ=0
    g25: LineSegment [constr] StartX=27.8417 StartY=8.13712 StartZ=0 EndX=27.8417 EndY=-1.46288 EndZ=0
    g26: LineSegment [constr] StartX=27.8417 StartY=-1.46288 StartZ=0 EndX=25.3417 EndY=-1.46288 EndZ=0
    g27: LineSegment [constr] StartX=25.3417 StartY=-1.46288 StartZ=0 EndX=25.3417 EndY=8.13712 EndZ=0
    g28: LineSegment [constr] StartX=25.3417 StartY=6.93712 StartZ=0 EndX=27.8417 EndY=6.93712 EndZ=0
    g29: LineSegment [constr] StartX=25.3417 StartY=5.73712 StartZ=0 EndX=27.8417 EndY=5.73712 EndZ=0
    g30: LineSegment [constr] StartX=25.3417 StartY=4.53712 StartZ=0 EndX=27.8417 EndY=4.53712 EndZ=0
    g31: LineSegment [constr] StartX=25.3417 StartY=3.33712 StartZ=0 EndX=27.8417 EndY=3.33712 EndZ=0
    g32: LineSegment [constr] StartX=25.3417 StartY=2.13712 StartZ=0 EndX=27.8417 EndY=2.13712 EndZ=0
    g33: LineSegment [constr] StartX=25.3417 StartY=0.937121 StartZ=0 EndX=27.8417 EndY=0.937121 EndZ=0
    g34: LineSegment [constr] StartX=25.3417 StartY=-0.262879 StartZ=0 EndX=27.8417 EndY=-0.262879 EndZ=0
    g35: ArcOfCircle CenterX=25.3417 CenterY=8.13712 CenterZ=0 NormalX=0 NormalY=0 NormalZ=1 AngleXU=0 Radius=0.75 StartAngle=1.12328 EndAngle=4.26487
    g36: ArcOfCircle CenterX=27.8417 CenterY=6.93712 CenterZ=0 NormalX=0 NormalY=0 NormalZ=1 AngleXU=0 Radius=0.75 StartAngle=4.26487 EndAngle=7.40646
    g37: Circle [constr] CenterX=27.8417 CenterY=6.93712 CenterZ=0 NormalX=0 NormalY=0 NormalZ=1 AngleXU=0 Radius=0.75
    g38: Circle [constr] CenterX=25.3417 CenterY=8.13712 CenterZ=0 NormalX=0 NormalY=0 NormalZ=1 AngleXU=0 Radius=0.75
    g39: LineSegment [constr] StartX=25.4338 StartY=8.92483 StartZ=0 EndX=28.7439 EndY=7.33601 EndZ=0
    g40: LineSegment [constr] StartX=24.2457 StartY=7.83129 StartZ=0 EndX=27.5618 EndY=6.23954 EndZ=0
    g41: LineSegment StartX=25.6663 StartY=8.81326 StartZ=0 EndX=28.1663 EndY=7.61326 EndZ=0
    g42: LineSegment StartX=25.0172 StartY=7.46098 StartZ=0 EndX=27.5172 EndY=6.26098 EndZ=0
    g43: ArcOfCircle CenterX=25.3417 CenterY=5.73712 CenterZ=0 NormalX=0 NormalY=0 NormalZ=1 AngleXU=0 Radius=0.75 StartAngle=1.12852 EndAngle=4.25962
    g44: LineSegment StartX=25.6627 StartY=6.41496 StartZ=0 EndX=28.149 EndY=5.22128 EndZ=0
    g45: ArcOfCircle CenterX=27.8417 CenterY=4.53712 CenterZ=0 NormalX=0 NormalY=0 NormalZ=1 AngleXU=0 Radius=0.75 StartAngle=4.23957 EndAngle=7.43184
    g46: LineSegment StartX=25.0136 StartY=5.06269 StartZ=0 EndX=27.5002 EndY=3.86941 EndZ=0
    g47: Circle CenterX=25.3417 CenterY=-1.46288 CenterZ=0 NormalX=0 NormalY=0 NormalZ=1 AngleXU=0 Radius=0.75
    g48: Circle CenterX=27.8417 CenterY=-0.262879 CenterZ=0 NormalX=0 NormalY=0 NormalZ=1 AngleXU=0 Radius=0.75
    g49: Circle CenterX=25.3417 CenterY=0.937121 CenterZ=0 NormalX=0 NormalY=0 NormalZ=1 AngleXU=0 Radius=0.75
    g50: Circle CenterX=27.8417 CenterY=2.13712 CenterZ=0 NormalX=0 NormalY=0 NormalZ=1 AngleXU=0 Radius=0.75
    g51: Circle CenterX=25.3417 CenterY=3.33712 CenterZ=0 NormalX=0 NormalY=0 NormalZ=1 AngleXU=0 Radius=0.75
    g52: LineSegment [constr] StartX=25.8911 StartY=-2.0311 StartZ=0 EndX=28.1814 EndY=-0.931754 EndZ=0
    g53: LineSegment [constr] StartX=24.1632 StartY=-1.19664 StartZ=0 EndX=27.4908 EndY=0.400624 EndZ=0
    g54: LineSegment [constr] StartX=24.363 StartY=0.574977 StartZ=0 EndX=28.2413 EndY=-1.28662 EndZ=0
    g55: LineSegment [constr] StartX=25.6678 StartY=1.61253 StartZ=0 EndX=28.5751 EndY=0.217016 EndZ=0
    g56: LineSegment [constr] StartX=24.9997 StartY=-0.0589725 StartZ=0 EndX=28.6995 EndY=1.71693 EndZ=0
    g57: LineSegment [constr] StartX=24.1511 StartY=1.19754 StartZ=0 EndX=27.2971 EndY=2.70762 EndZ=0
    g58: LineSegment [constr] StartX=24.3738 StartY=2.96979 StartZ=0 EndX=27.5399 EndY=1.45005 EndZ=0
    g59: Circle [constr] CenterX=25.3417 CenterY=2.13712 CenterZ=0 NormalX=0 NormalY=0 NormalZ=1 AngleXU=0 Radius=0.331828
    g60: Circle [constr] CenterX=27.8417 CenterY=0.937121 CenterZ=0 NormalX=0 NormalY=0 NormalZ=1 AngleXU=0 Radius=0.331828
    g61: Circle [constr] CenterX=25.3417 CenterY=-0.262879 CenterZ=0 NormalX=0 NormalY=0 NormalZ=1 AngleXU=0 Radius=0.331828
  constraints (163):
    c: Coincident(g0,g1)
    c: Coincident(g1,g2)
    c: Coincident(g2,g3)
    c: Coincident(g3,g0)
    c: Horizontal(g2)
    c: Vertical(g3)
    c: DistanceX(g0,g0) = 65
    c: DistanceY(g1,g1) = 30
    c: Symmetric(g0,g0,g-2)
    c: Symmetric(g0,g1,g-1)
    c: Coincident(g4,g5)
    c: Coincident(g5,g6)
    c: Coincident(g6,g7)
    c: Coincident(g7,g4)
    c: Horizontal(g4)
    c: Horizontal(g6)
    c: Vertical(g5)
    c: Vertical(g7)
    c: DistanceX(g4,g4) = 58
    c: DistanceY(g5,g5) = 23
    c: Symmetric(g4,g5,g-1)
    c: Symmetric(g4,g4,g-2)
    c: Coincident(g8,g4)
    c: Coincident(g9,g4)
    c: Coincident(g10,g5)
    c: Coincident(g11,g6)
    c: Radius(g11) = 1.375
    c: Radius(g8) = 1.375
    c: Radius(g9) = 1.375
    c: Radius(g10) = 1.375
    c: Coincident(g12,g13)
    c: Coincident(g13,g14)
    c: Coincident(g14,g15)
    c: Coincident(g15,g12)
    c: Horizontal(g12)
    c: Horizontal(g14)
    c: Vertical(g13)
    c: Vertical(g15)
    c: DistanceX(g4,g12) = 0.5
    c: DistanceY(g4,g12) = 0.5
    c: DistanceY(g13,g5) = 0.5
    c: DistanceX(g14,g6) = 0.5
    c: Coincident(g16,g12)
    c: Radius(g16) = 3
    c: Coincident(g17,g12)
    c: Radius(g17) = 3
    c: Coincident(g18,g13)
    c: Radius(g18) = 3
    c: Coincident(g19,g14)
    c: Radius(g19) = 3
    c: PointOnObject(g16,g0)
    c: PointOnObject(g17,g1)
    c: PointOnObject(g18,g2)
    c: PointOnObject(g19,g3)
    c: Coincident(g20,g16)
    c: Horizontal(g20)
    c: Coincident(g20,g17)
    c: Coincident(g21,g17)
    c: Vertical(g21)
    c: Coincident(g18,g21)
    c: Coincident(g22,g18)
    c: Horizontal(g22)
    c: Coincident(g19,g22)
    c: Coincident(g23,g19)
    c: Vertical(g23)
    c: Coincident(g23,g16)
    c: Coincident(g24,g25)
    c: Coincident(g25,g26)
    c: Coincident(g26,g27)
    c: Coincident(g27,g24)
    c: Horizontal(g24)
    c: Horizontal(g26)
    c: Vertical(g25)
    c: Vertical(g27)
    c: DistanceX(g4,g24) = 54.3417  '3,362879'
    c: DistanceX(g24,g24) = 2.5
    c: DistanceY(g27,g27) = 9.6
    c: DistanceY(g24,g4) = 3.36288
    c: Horizontal(g28)
    c: Horizontal(g29)
    c: Horizontal(g30)
    c: Horizontal(g32)
    c: Horizontal(g33)
    c: DistanceY(g28,g24) = 1.2
    c: DistanceY(g29,g28) = 1.2
    c: DistanceY(g30,g29) = 1.2
    c: DistanceY(g31,g30) = 1.2
    c: DistanceY(g32,g31) = 1.2
    c: DistanceY(g33,g32) = 1.2
    c: Horizontal(g34)
    c: DistanceY(g34,g33) = 1.2
    c: PointOnObject(g28,g27)
    c: PointOnObject(g29,g27)
    c: PointOnObject(g30,g27)
    c: PointOnObject(g31,g27)
    c: PointOnObject(g32,g27)
    c: PointOnObject(g33,g27)
    c: PointOnObject(g34,g27)
    c: PointOnObject(g34,g25)
    c: PointOnObject(g33,g25)
    c: PointOnObject(g32,g25)
    c: PointOnObject(g31,g25)
    c: PointOnObject(g30,g25)
    c: PointOnObject(g29,g25)
    c: PointOnObject(g28,g25)
    c: Coincident(g35,g24)
    c: Coincident(g36,g28)
    c: Radius(g35) = 0.75
    c: Radius(g36) = 0.75
    c: Coincident(g37,g28)
    c: Coincident(g38,g24)
    c: Radius(g38) = 0.75
    c: Radius(g37) = 0.75
    c: Tangent(g39,g37)
    c: Tangent(g39,g38)
    c: Tangent(g40,g38)
    c: Tangent(g40,g37)
    c: PointOnObject(g41,g39)
    c: PointOnObject(g41,g39)
    c: PointOnObject(g42,g40)
    c: PointOnObject(g42,g40)
    c: Coincident(g41,g35)
    c: Coincident(g35,g42)
    c: Coincident(g41,g36)
    c: Coincident(g36,g42)
    c: Equal(g35,g43) = 0.75
    c: Equal(g36,g45) = 0.75
    c: Coincident(g44,g43)
    c: Coincident(g43,g46)
    c: Coincident(g44,g45)
    c: Coincident(g45,g46)
    c: Coincident(g43,g29)
    c: Coincident(g45,g30)
    c: Coincident(g48,g34)
    c: Coincident(g49,g33)
    c: Coincident(g50,g32)
    c: Coincident(g51,g31)
    c: Radius(g51) = 0.75
    c: Radius(g50) = 0.75
    c: Radius(g49) = 0.75
    c: Radius(g48) = 0.75
    c: Radius(g47) = 0.75
    c: Tangent(g55,g48)
    c: Tangent(g55,g49)
    c: Tangent(g54,g49)
    c: Tangent(g54,g48)
    c: Tangent(g53,g47)
    c: Tangent(g53,g48)
    c: Coincident(g47,g26)
    c: Tangent(g47,g52)
    c: Tangent(g52,g48)
    c: Tangent(g56,g49)
    c: Tangent(g56,g50)
    c: Tangent(g57,g50)
    c: Tangent(g57,g49)
    c: Tangent(g58,g51)
    c: Tangent(g58,g50)
    c: Coincident(g59,g32)
    c: Tangent(g59,g58)
    c: Coincident(g60,g33)
    c: Tangent(g60,g56)
    c: Coincident(g61,g34)
    c: Tangent(g61,g54)
FEATURE [PartDesign::Pocket] Pocket005
  BaseFeature = -> Pocket004
  Length = 5
  Length2 = 100
  Profile = -> Sketch009
  Type = 2
FEATURE [Part::Feature] path76
  shape: bbox 67.53 x 33.36 x 2e-07 mm, 1 faces, 0 solids (baked)
FEATURE [Part::Feature] path76001
  shape: bbox 56.51 x 33.36 x 2e-07 mm, 1 faces, 0 solids (baked)
FEATURE [Part::Feature] path76002
  shape: bbox 67.23 x 33.39 x 2e-07 mm, 1 faces, 0 solids (baked)
FEATURE [Part::Feature] path76003
  shape: bbox 86.8 x 33.05 x 2e-07 mm, 1 faces, 0 solids (baked)
FEATURE [Part::Feature] path76004
  shape: bbox 24.36 x 17.06 x 2e-07 mm, 1 faces, 0 solids (baked)
FEATURE [Part::Cut] Cut
  Base = -> path76003
  Tool = -> path76004
FEATURE [Part::MultiFuse] Fusion
  Shapes = -> [path76,path76001,path76002,Cut]
FEATURE [Part::FeaturePython] Scale001  # Draft clone (typed FeaturePython)
  Fuse = false
  Objects = -> [Fusion]
  Placement = pos=(-20,0,14.85) rot=(0,0,1;0rad)
  Scale = (0.18,0.18,0.18)
FEATURE [Part::FeaturePython] Scale  # Draft clone (typed FeaturePython)
  Fuse = false
  Objects = -> [Scale001]
  Placement = pos=(-11.9,-2.3,14.95) rot=(0,0,1;0rad)
  Scale = (0.8,0.8,0.8)
FEATURE [PartDesign::Fillet] Fillet001
  Base = -> Pocket005 [Edge33,Edge21,Edge22,Edge34,Edge20,Edge23,Edge27,Edge116,Edge88,Edge114,Edge90,Edge92,Edge99,Edge107]
  BaseFeature = -> Pocket005
  Radius = 0.2
FEATURE [PartDesign::Fillet] Fillet002
  Base = -> Fillet001 [Edge22,Edge28,Edge27,Edge21]
  BaseFeature = -> Fillet001
  Radius = 0.1
FEATURE [PartDesign::Fillet] Fillet004
  Base = -> Fillet002 [Edge246,Edge241,Edge245,Edge247,Edge233]
  BaseFeature = -> Fillet002
  Radius = 0.1
FEATURE [PartDesign::Body] Body
  Group = -> [Sketch,Sketch001,Pad,Sketch002,Pocket,Sketch003,Pocket001,Sketch004,Sketch005,Pocket002,Sketch006,Pocket003,Fillet,Chamfer,Sketch007,Hole,Sketch008,Pocket004,Sketch009,Pocket005,Fillet001,Fillet002,Fillet004]
  Origin = -> Origin
  Tip = -> Fillet004
FEATURE [Part::Extrusion] Extrude
  Base = -> Scale
  Dir = (0,0,1)
  DirMode = 0
  FaceMakerClass = Part::FaceMakerBullseye
  LengthFwd = 5
  LengthRev = 0
  Solid = false
  Symmetric = false
FEATURE [Part::Cut] Cut001
  Base = -> Fillet004
  Tool = -> Extrude
FEATURE [Mesh::Feature] Mesh  label="Cut001 (Meshed)"
